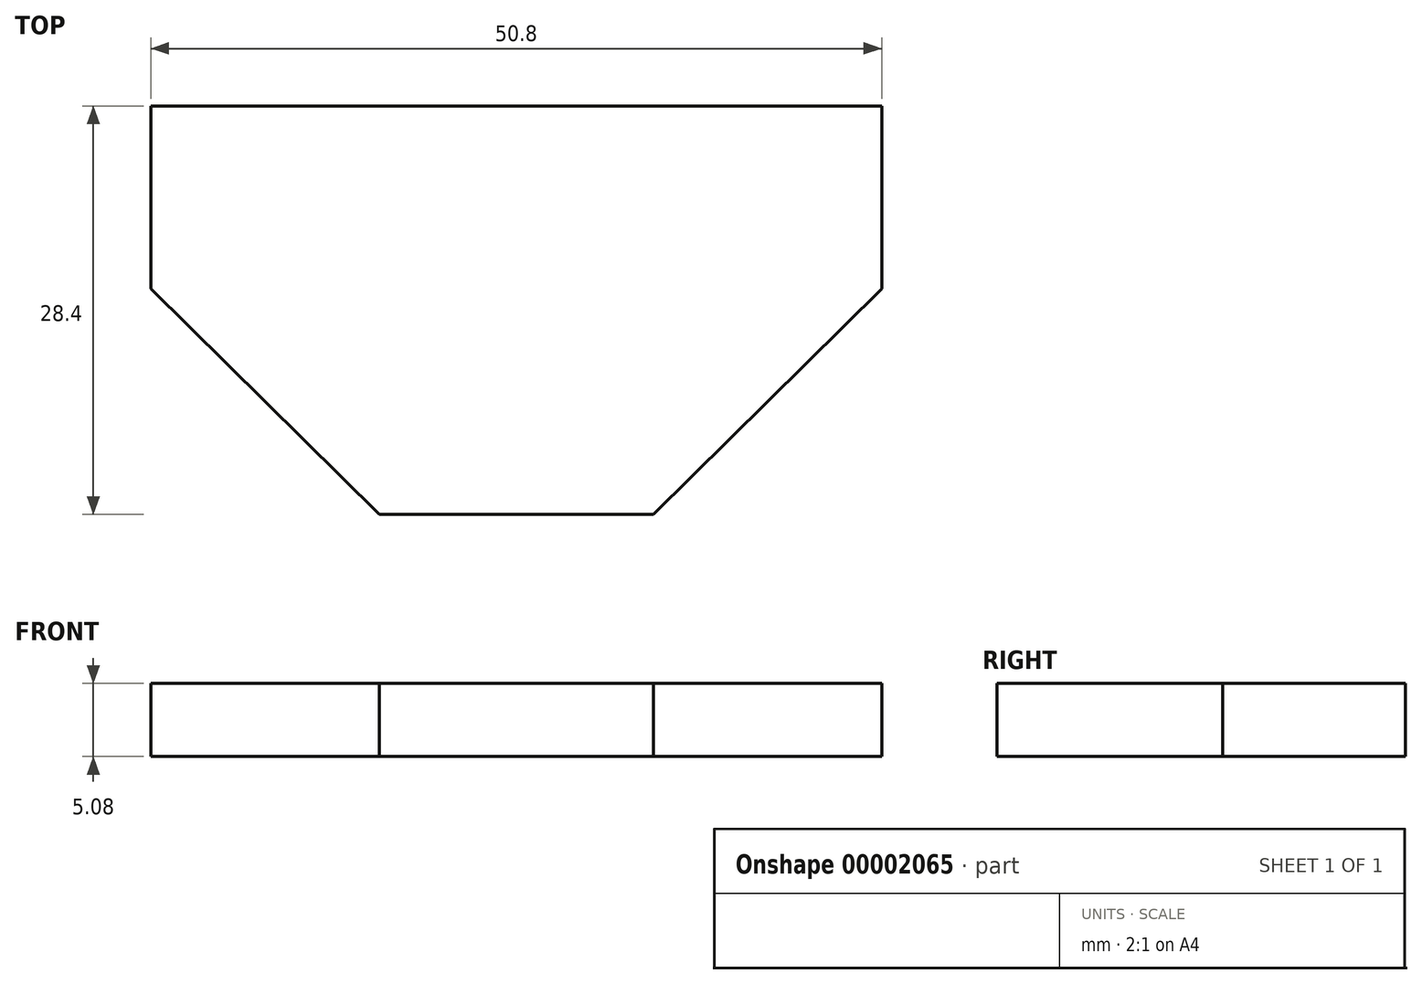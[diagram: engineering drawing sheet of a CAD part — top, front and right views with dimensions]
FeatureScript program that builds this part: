
annotation { "Feature Type Name" : "Feature", "Feature Type Description" : "" }
export const myFeature = defineFeature(function(context is Context, id is Id, definition is map)
    precondition{}
    {
        {
            var Q0;
            Q0=qCreatedBy(makeId("Top.planeOp"),FACE);
            var sketch = newSketch(context, id + "F0", { "sketchPlane" : qUnion([Q0])});
            skLineSegment(sketch, "E0", {"start": v(-25.4, 28.4) * mm, "end": v(25.4, 28.4) * mm});
            skLineSegment(sketch, "E1", {"start": v(25.4, 28.4) * mm, "end": v(25.4, 15.7) * mm});
            skLineSegment(sketch, "E2", {"start": v(25.4, 15.7) * mm, "end": v(9.52, 0) * mm});
            skLineSegment(sketch, "E3", {"start": v(9.53, 0) * mm, "end": v(-9.53, 0) * mm});
            skLineSegment(sketch, "E4", {"start": v(-9.53, 0) * mm, "end": v(-25.4, 15.7) * mm});
            skLineSegment(sketch, "E5", {"start": v(-25.4, 15.7) * mm, "end": v(-25.4, 28.4) * mm});
            skSolve(sketch);
        }
        {
            var Q0;
            Q0=makeQuery(id+"F0.imprint","IMPRINT",FACE,{"disambiguationData":[TD([[makeQuery(id+"F0.imprint","IMPRINT",EDGE,{"derivedFrom":sQuery(id+"F0.wireOp",EDGE,"E0")}),-1.0]])]});
            extrude(context, id + "F1", {"entities" : qUnion([Q0]), "depth" : 5.08 * mm});
        }
    });
